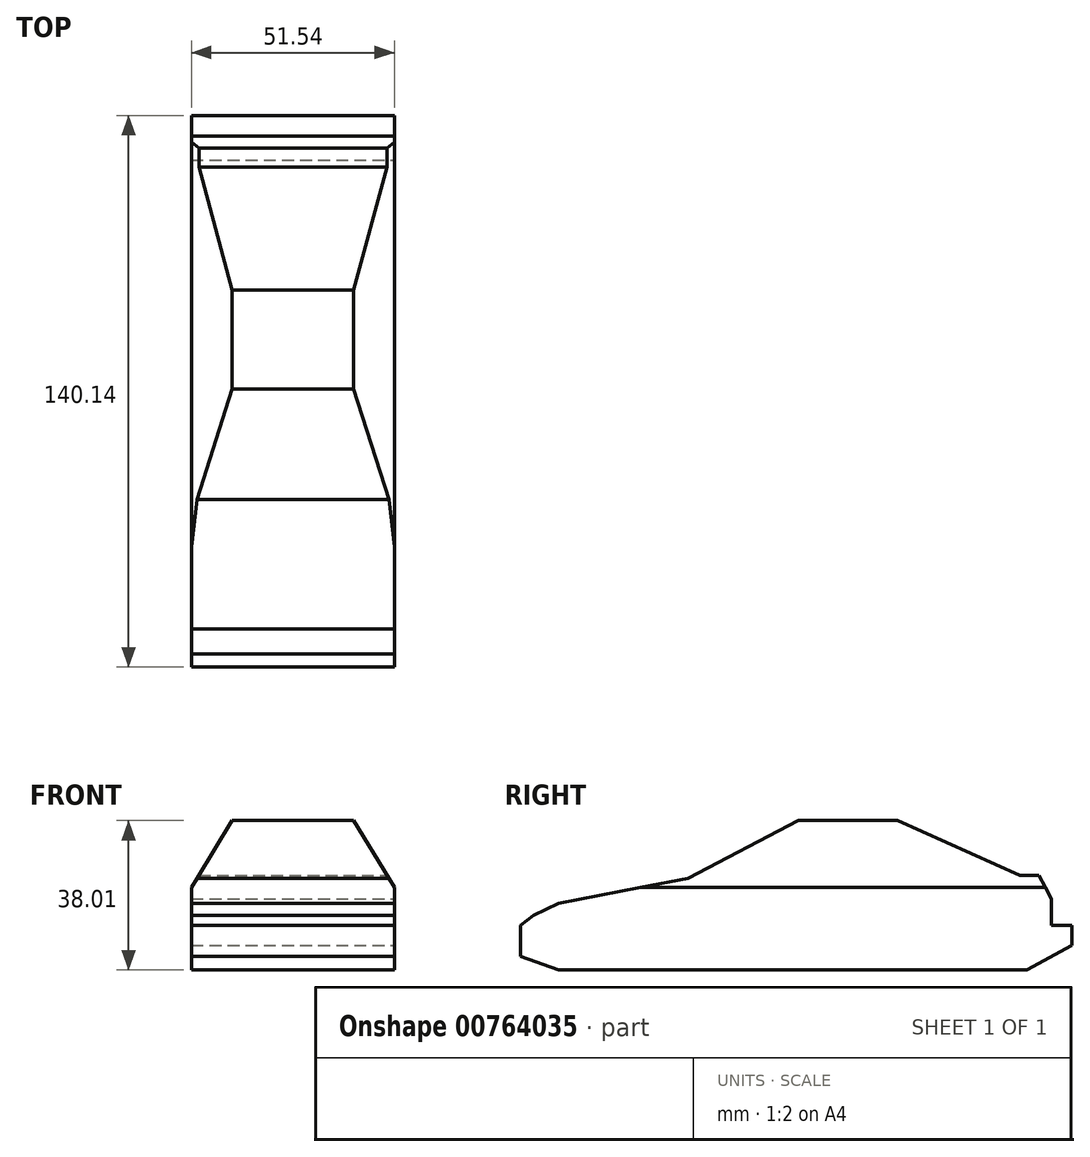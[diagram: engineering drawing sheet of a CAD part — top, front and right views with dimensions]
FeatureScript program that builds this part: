
annotation { "Feature Type Name" : "Feature", "Feature Type Description" : "" }
export const myFeature = defineFeature(function(context is Context, id is Id, definition is map)
    precondition{}
    {
        {
            var Q0;
            Q0=qCreatedBy(makeId("Front.planeOp"),FACE);
            var sketch = newSketch(context, id + "F0", { "sketchPlane" : qUnion([Q0])});
            skLineSegment(sketch, "E0", {"start": v(0, 0) * mm, "end": v(-25.77, 0) * mm});
            skLineSegment(sketch, "E1", {"start": v(-25.77, 0) * mm, "end": v(-25.77, 24.28) * mm});
            skLineSegment(sketch, "E2", {"start": v(-25.77, 24.28) * mm, "end": v(-6.38, 56.12) * mm});
            skLineSegment(sketch, "E3", {"start": v(-6.38, 56.12) * mm, "end": v(0, 56.12) * mm});
            skLineSegment(sketch, "E4.MirrorCS", {"start": v(25.77, 24.28) * mm, "end": v(6.38, 56.12) * mm});
            skLineSegment(sketch, "E5.MirrorCS", {"start": v(25.77, 0) * mm, "end": v(25.77, 24.28) * mm});
            skLineSegment(sketch, "E6.MirrorCS", {"start": v(0, 0) * mm, "end": v(25.77, 0) * mm});
            skLineSegment(sketch, "E7.MirrorCS", {"start": v(6.38, 56.12) * mm, "end": v(0, 56.12) * mm});
            skSolve(sketch);
        }
        {
            var Q0;
            Q0=makeQuery(id+"F0.imprint","IMPRINT",FACE,{"disambiguationData":[TD([[makeQuery(id+"F0.imprint","IMPRINT",EDGE,{"derivedFrom":sQuery(id+"F0.wireOp",EDGE,"E0")}),-1.0]])]});
            extrude(context, id + "F1", {"entities" : qUnion([Q0]), "depth" : 150.62 * mm, "offsetDistance" : 25.4 * mm});
        }
        {
            var Q0;
            Q0=qCreatedBy(makeId("Right.planeOp"),FACE);
            var sketch = newSketch(context, id + "F2", { "sketchPlane" : qUnion([Q0])});
            skLineSegment(sketch, "E8", {"start": v(-151.6, 7.1) * mm, "end": v(-151.6, 13.94) * mm});
            skLineSegment(sketch, "E9", {"start": v(-151.6, 13.94) * mm, "end": v(-147.3, 17.23) * mm});
            skLineSegment(sketch, "E10", {"start": v(-147.3, 17.23) * mm, "end": v(-140.96, 20.27) * mm});
            skLineSegment(sketch, "E11", {"start": v(-140.96, 20.27) * mm, "end": v(-108.03, 26.6) * mm});
            skLineSegment(sketch, "E12", {"start": v(-108.03, 26.6) * mm, "end": v(-79.97, 41.3) * mm});
            skLineSegment(sketch, "E13", {"start": v(-79.97, 41.3) * mm, "end": v(-54.82, 41.3) * mm});
            skLineSegment(sketch, "E14", {"start": v(-54.82, 41.3) * mm, "end": v(-23.66, 27.36) * mm});
            skLineSegment(sketch, "E15", {"start": v(-23.66, 27.36) * mm, "end": v(-18.84, 27.36) * mm});
            skLineSegment(sketch, "E16", {"start": v(-18.84, 27.36) * mm, "end": v(-15.7, 21.35) * mm});
            skLineSegment(sketch, "E17", {"start": v(-15.7, 21.35) * mm, "end": v(-15.7, 14.7) * mm});
            skLineSegment(sketch, "E18", {"start": v(-15.7, 14.7) * mm, "end": v(-10.48, 14.7) * mm});
            skLineSegment(sketch, "E19", {"start": v(-10.48, 14.7) * mm, "end": v(-10.48, 9.63) * mm});
            skLineSegment(sketch, "E20", {"start": v(-10.48, 9.63) * mm, "end": v(-21.88, 3.3) * mm});
            skLineSegment(sketch, "E21", {"start": v(-21.88, 3.3) * mm, "end": v(-140.88, 3.3) * mm});
            skLineSegment(sketch, "E22", {"start": v(-140.88, 3.3) * mm, "end": v(-151.6, 7.1) * mm});
            skSolve(sketch);
        }
        {
            var Q0;
            Q0 = qSketchRegion(id + "F2", true);
            extrude(context, id + "F3", {"entities" : qUnion([Q0]), "operationType" : NewBodyOperationType.INTERSECT, "endBound" : BoundingType.THROUGH_ALL, "oppositeDirection" : true, "depth" : 97.54 * mm, "offsetDistance" : 25.4 * mm, "hasSecondDirection" : true, "secondDirectionOppositeDirection" : false, "secondDirectionDepth" : 88.4 * mm});
        }
    });
